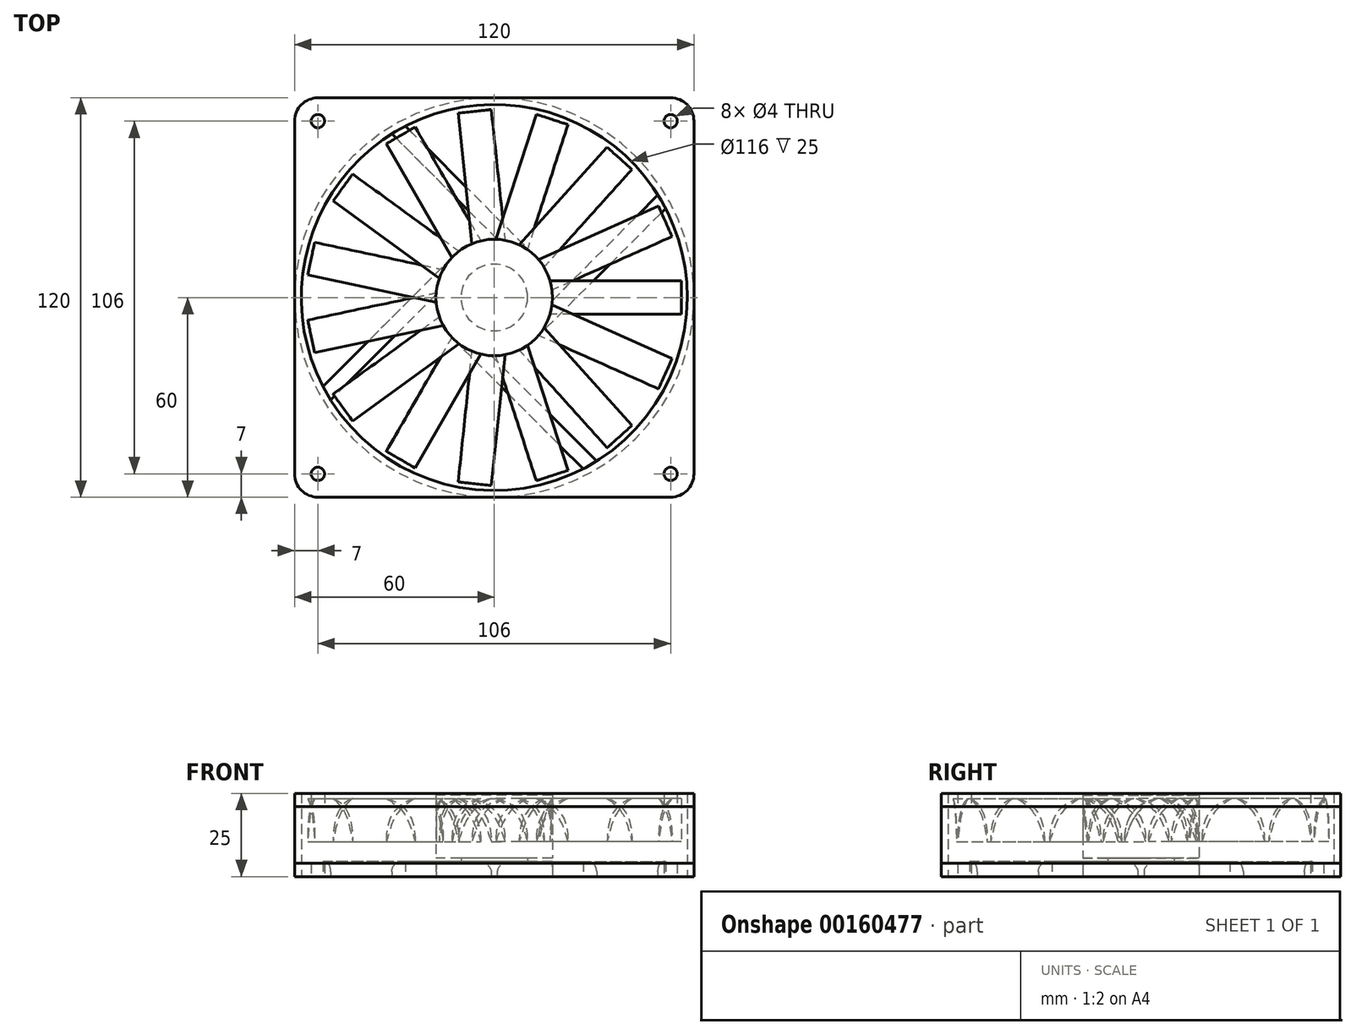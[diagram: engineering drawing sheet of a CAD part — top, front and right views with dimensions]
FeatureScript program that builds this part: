
annotation { "Feature Type Name" : "Feature", "Feature Type Description" : "" }
export const myFeature = defineFeature(function(context is Context, id is Id, definition is map)
    precondition{}
    {
        {
            var Q0;
            Q0=qCreatedBy(makeId("Top.planeOp"),FACE);
            var sketch = newSketch(context, id + "F0", { "sketchPlane" : qUnion([Q0])});
            skLineSegment(sketch, "E0.bottom", {"start": v(-60, 60) * mm, "end": v(60, 60) * mm});
            skLineSegment(sketch, "E0.top", {"start": v(-60, -60) * mm, "end": v(60, -60) * mm});
            skLineSegment(sketch, "E0.left", {"start": v(-60, 60) * mm, "end": v(-60, -60) * mm});
            skLineSegment(sketch, "E0.right", {"start": v(60, 60) * mm, "end": v(60, -60) * mm});
            skCircle(sketch, "E1", {"center": v(0, 0) * mm, "radius": 60 * mm});
            skPoint(sketch, "E2.positionSnap0", {"position": v(0, -60) * mm});
            skPoint(sketch, "E2.positionSnap1", {"position": v(60, 0) * mm});
            skCircle(sketch, "E3", {"center": v(0, 0) * mm, "radius": 58 * mm});
            skSolve(sketch);
        }
        {
            var Q0;
            {var subQ0=sQuery(id+"F0.wireOp",EDGE,"E1");var subQ1=makeQuery(id+"F0.imprint","INTERSECT",VERTEX,{"derivedFrom":[sQuery(id+"F0.wireOp",EDGE,"E0.bottom"),subQ0]});Q0=makeQuery(id+"F0.imprint","IMPRINT",FACE,{"disambiguationData":[TD([[makeQuery(id+"F0.imprint","IMPRINT",EDGE,{"disambiguationData":[TD([[subQ1,1.0]])],"derivedFrom":subQ0}),1.0]])]});}
            extrude(context, id + "F1", {"entities" : qUnion([Q0]), "depth" : 25 * mm});
        }
        {
            var Q0;
            {var subQ0=sQuery(id+"F0.wireOp",EDGE,"E0.left");var subQ1=sQuery(id+"F0.wireOp",EDGE,"E0.bottom");var subQ2=makeQuery(id+"F0.imprint","INTERSECT",VERTEX,{"derivedFrom":[subQ1,subQ0]});Q0=makeQuery(id+"F0.imprint","IMPRINT",FACE,{"disambiguationData":[TD([[makeQuery(id+"F0.imprint","IMPRINT",EDGE,{"disambiguationData":[TD([[subQ2,-1.0]])],"derivedFrom":subQ1}),-1.0]])]});}
            var Q1;
            {var subQ0=sQuery(id+"F0.wireOp",EDGE,"E0.right");var subQ1=sQuery(id+"F0.wireOp",EDGE,"E0.bottom");var subQ2=makeQuery(id+"F0.imprint","INTERSECT",VERTEX,{"derivedFrom":[subQ1,subQ0]});Q1=makeQuery(id+"F0.imprint","IMPRINT",FACE,{"disambiguationData":[TD([[makeQuery(id+"F0.imprint","IMPRINT",EDGE,{"disambiguationData":[TD([[subQ2,1.0]])],"derivedFrom":subQ1}),-1.0]])]});}
            var Q2;
            {var subQ0=sQuery(id+"F0.wireOp",EDGE,"E0.right");var subQ1=sQuery(id+"F0.wireOp",EDGE,"E0.top");var subQ2=makeQuery(id+"F0.imprint","INTERSECT",VERTEX,{"derivedFrom":[subQ1,subQ0]});Q2=makeQuery(id+"F0.imprint","IMPRINT",FACE,{"disambiguationData":[TD([[makeQuery(id+"F0.imprint","IMPRINT",EDGE,{"disambiguationData":[TD([[subQ2,1.0]])],"derivedFrom":subQ1}),1.0]])]});}
            var Q3;
            {var subQ0=sQuery(id+"F0.wireOp",EDGE,"E0.left");var subQ1=sQuery(id+"F0.wireOp",EDGE,"E0.top");var subQ2=makeQuery(id+"F0.imprint","INTERSECT",VERTEX,{"derivedFrom":[subQ1,subQ0]});Q3=makeQuery(id+"F0.imprint","IMPRINT",FACE,{"disambiguationData":[TD([[makeQuery(id+"F0.imprint","IMPRINT",EDGE,{"disambiguationData":[TD([[subQ2,-1.0]])],"derivedFrom":subQ1}),1.0]])]});}
            extrude(context, id + "F2", {"entities" : qUnion([Q0, Q1, Q2, Q3]), "operationType" : NewBodyOperationType.ADD, "depth" : 4 * mm});
        }
        {
            var Q0;
            Q0=makeQuery(id+"F1.opExtrude","CAP_FACE",FACE,{"disambiguationData":[OSD([sQuery(id+"F0.wireOp",EDGE,"E1"),sQuery(id+"F0.wireOp",EDGE,"E3")])],"isStart":false});
            var sketch = newSketch(context, id + "F3", { "sketchPlane" : qUnion([Q0])});
            skLineSegment(sketch, "E4.0", {"start": v(-60, -60) * mm, "end": v(60, -60) * mm});
            skLineSegment(sketch, "E5.0", {"start": v(-60, 60) * mm, "end": v(-60, -60) * mm});
            skLineSegment(sketch, "E6.0", {"start": v(-60, 60) * mm, "end": v(60, 60) * mm});
            skLineSegment(sketch, "E7.0", {"start": v(60, 60) * mm, "end": v(60, -60) * mm});
            skSolve(sketch);
        }
        {
            var Q0;
            {var subQ0=sQuery(id+"F3.wireOp",EDGE,"E7.0");var subQ1=sQuery(id+"F3.wireOp",EDGE,"E4.0");var subQ2=makeQuery(id+"F3.imprint","INTERSECT",VERTEX,{"derivedFrom":[subQ1,subQ0]});Q0=makeQuery(id+"F3.imprint","IMPRINT",FACE,{"disambiguationData":[TD([[makeQuery(id+"F3.imprint","IMPRINT",EDGE,{"disambiguationData":[TD([[subQ2,1.0]])],"derivedFrom":subQ1}),1.0]])]});}
            var Q1;
            {var subQ0=sQuery(id+"F3.wireOp",EDGE,"E7.0");var subQ1=sQuery(id+"F3.wireOp",EDGE,"E6.0");var subQ2=makeQuery(id+"F3.imprint","INTERSECT",VERTEX,{"derivedFrom":[subQ1,subQ0]});Q1=makeQuery(id+"F3.imprint","IMPRINT",FACE,{"disambiguationData":[TD([[makeQuery(id+"F3.imprint","IMPRINT",EDGE,{"disambiguationData":[TD([[subQ2,1.0]])],"derivedFrom":subQ1}),-1.0]])]});}
            var Q2;
            {var subQ0=sQuery(id+"F3.wireOp",EDGE,"E5.0");var subQ1=sQuery(id+"F3.wireOp",EDGE,"E4.0");var subQ2=makeQuery(id+"F3.imprint","INTERSECT",VERTEX,{"derivedFrom":[subQ1,subQ0]});Q2=makeQuery(id+"F3.imprint","IMPRINT",FACE,{"disambiguationData":[TD([[makeQuery(id+"F3.imprint","IMPRINT",EDGE,{"disambiguationData":[TD([[subQ2,-1.0]])],"derivedFrom":subQ1}),1.0]])]});}
            var Q3;
            {var subQ0=sQuery(id+"F3.wireOp",EDGE,"E6.0");var subQ1=sQuery(id+"F3.wireOp",EDGE,"E5.0");var subQ2=makeQuery(id+"F3.imprint","INTERSECT",VERTEX,{"derivedFrom":[subQ1,subQ0]});Q3=makeQuery(id+"F3.imprint","IMPRINT",FACE,{"disambiguationData":[TD([[makeQuery(id+"F3.imprint","IMPRINT",EDGE,{"disambiguationData":[TD([[subQ2,-1.0]])],"derivedFrom":subQ1}),1.0]])]});}
            extrude(context, id + "F4", {"entities" : qUnion([Q0, Q1, Q2, Q3]), "operationType" : NewBodyOperationType.ADD, "oppositeDirection" : true, "depth" : 4 * mm});
        }
        {
            var Q0;
            Q0=makeQuery(id+"F4.opExtrude","SWEPT_EDGE",EDGE,{"disambiguationData":[OSD([sQuery(id+"F3.wireOp",EDGE,"E4.0"),sQuery(id+"F3.wireOp",EDGE,"E5.0")])]});
            var Q1;
            Q1=makeQuery(id+"F2.opExtrude","SWEPT_EDGE",EDGE,{"disambiguationData":[OSD([sQuery(id+"F0.wireOp",EDGE,"E0.top"),sQuery(id+"F0.wireOp",EDGE,"E0.left")])]});
            var Q2;
            Q2=makeQuery(id+"F4.opExtrude","SWEPT_EDGE",EDGE,{"disambiguationData":[OSD([sQuery(id+"F3.wireOp",EDGE,"E5.0"),sQuery(id+"F3.wireOp",EDGE,"E6.0")])]});
            var Q3;
            Q3=makeQuery(id+"F2.opExtrude","SWEPT_EDGE",EDGE,{"disambiguationData":[OSD([sQuery(id+"F0.wireOp",EDGE,"E0.bottom"),sQuery(id+"F0.wireOp",EDGE,"E0.left")])]});
            var Q4;
            Q4=makeQuery(id+"F2.opExtrude","SWEPT_EDGE",EDGE,{"disambiguationData":[OSD([sQuery(id+"F0.wireOp",EDGE,"E0.bottom"),sQuery(id+"F0.wireOp",EDGE,"E0.right")])]});
            var Q5;
            Q5=makeQuery(id+"F4.opExtrude","SWEPT_EDGE",EDGE,{"disambiguationData":[OSD([sQuery(id+"F3.wireOp",EDGE,"E6.0"),sQuery(id+"F3.wireOp",EDGE,"E7.0")])]});
            var Q6;
            Q6=makeQuery(id+"F4.opExtrude","SWEPT_EDGE",EDGE,{"disambiguationData":[OSD([sQuery(id+"F3.wireOp",EDGE,"E4.0"),sQuery(id+"F3.wireOp",EDGE,"E7.0")])]});
            var Q7;
            Q7=makeQuery(id+"F2.opExtrude","SWEPT_EDGE",EDGE,{"disambiguationData":[OSD([sQuery(id+"F0.wireOp",EDGE,"E0.top"),sQuery(id+"F0.wireOp",EDGE,"E0.right")])]});
            fillet(context, id + "F5", {"entities" : qUnion([Q0, Q1, Q2, Q3, Q4, Q5, Q6, Q7]), "radius" : 7 * mm, "tangentPropagation" : true, "allowEdgeOverflow" : false});
        }
        {
            var Q0;
            {var subQ0=sQuery(id+"F0.wireOp",EDGE,"E0.left");var subQ1=sQuery(id+"F0.wireOp",EDGE,"E0.bottom");var subQ2=makeQuery(id+"F0.imprint","INTERSECT",VERTEX,{"derivedFrom":[subQ1,subQ0]});Q0=makeQuery(id+"F0.imprint","IMPRINT",FACE,{"disambiguationData":[TD([[makeQuery(id+"F0.imprint","IMPRINT",EDGE,{"disambiguationData":[TD([[subQ2,-1.0]])],"derivedFrom":subQ1}),-1.0]])]});}
            var sketch = newSketch(context, id + "F6", { "sketchPlane" : qUnion([Q0])});
            skLineSegment(sketch, "E8.bottom", {"start": v(-53, 53) * mm, "end": v(53, 53) * mm, "construction": true});
            skLineSegment(sketch, "E8.top", {"start": v(-53, -53) * mm, "end": v(53, -53) * mm, "construction": true});
            skLineSegment(sketch, "E8.left", {"start": v(-53, 53) * mm, "end": v(-53, -53) * mm, "construction": true});
            skLineSegment(sketch, "E8.right", {"start": v(53, 53) * mm, "end": v(53, -53) * mm, "construction": true});
            skCircle(sketch, "E9", {"center": v(-53, 53) * mm, "radius": 2 * mm});
            skCircle(sketch, "E10", {"center": v(-53, -53) * mm, "radius": 2 * mm});
            skCircle(sketch, "E11", {"center": v(53, -53) * mm, "radius": 2 * mm});
            skCircle(sketch, "E12", {"center": v(53, 53) * mm, "radius": 2 * mm});
            skSolve(sketch);
        }
        {
            var Q0;
            Q0=makeQuery(id+"F6.imprint","IMPRINT",FACE,{"disambiguationData":[TD([[makeQuery(id+"F6.imprint","IMPRINT",EDGE,{"derivedFrom":sQuery(id+"F6.wireOp",EDGE,"E9")}),1.0]])]});
            var Q1;
            Q1=makeQuery(id+"F6.imprint","IMPRINT",FACE,{"disambiguationData":[TD([[makeQuery(id+"F6.imprint","IMPRINT",EDGE,{"derivedFrom":sQuery(id+"F6.wireOp",EDGE,"E10")}),1.0]])]});
            var Q2;
            Q2=makeQuery(id+"F6.imprint","IMPRINT",FACE,{"disambiguationData":[TD([[makeQuery(id+"F6.imprint","IMPRINT",EDGE,{"derivedFrom":sQuery(id+"F6.wireOp",EDGE,"E12")}),1.0]])]});
            var Q3;
            Q3=makeQuery(id+"F6.imprint","IMPRINT",FACE,{"disambiguationData":[TD([[makeQuery(id+"F6.imprint","IMPRINT",EDGE,{"derivedFrom":sQuery(id+"F6.wireOp",EDGE,"E11")}),1.0]])]});
            var Q4;
            Q4=sQuery(id+"F6.wireOp",EDGE,"E9");
            var Q5;
            Q5=sQuery(id+"F6.wireOp",EDGE,"E10");
            var Q6;
            Q6=sQuery(id+"F6.wireOp",EDGE,"E11");
            var Q7;
            Q7=sQuery(id+"F6.wireOp",EDGE,"E12");
            extrude(context, id + "F7", {"entities" : qUnion([Q0, Q1, Q2, Q3]), "operationType" : NewBodyOperationType.REMOVE, "surfaceEntities" : qUnion([Q4, Q5, Q6, Q7]), "depth" : 25 * mm});
        }
        {
            var Q0;
            Q0=qCreatedBy(makeId("Top.planeOp"),FACE);
            var sketch = newSketch(context, id + "F8", { "sketchPlane" : qUnion([Q0])});
            skCircle(sketch, "E13", {"center": v(0, 0) * mm, "radius": 17.5 * mm});
            skLineSegment(sketch, "E14", {"start": v(12.37, 12.37) * mm, "end": v(-26.73, 51.48) * mm});
            skLineSegment(sketch, "E15", {"start": v(0.9, 17.48) * mm, "end": v(-30.78, 49.16) * mm});
            skLineSegment(sketch, "E16.1.0", {"start": v(-17.48, 0.9) * mm, "end": v(-49.16, -30.78) * mm});
            skLineSegment(sketch, "E16.1.1", {"start": v(-12.37, 12.37) * mm, "end": v(-51.48, -26.73) * mm});
            skLineSegment(sketch, "E16.2.0", {"start": v(-0.9, -17.48) * mm, "end": v(30.78, -49.16) * mm});
            skLineSegment(sketch, "E16.2.1", {"start": v(-12.37, -12.37) * mm, "end": v(26.73, -51.48) * mm});
            skLineSegment(sketch, "E16.3.0", {"start": v(17.48, -0.9) * mm, "end": v(49.16, 30.78) * mm});
            skLineSegment(sketch, "E16.3.1", {"start": v(12.37, -12.37) * mm, "end": v(51.48, 26.73) * mm});
            skCircle(sketch, "E17", {"center": v(0, 0) * mm, "radius": 58 * mm});
            skSolve(sketch);
        }
        {
            var Q0;
            {var subQ0=sQuery(id+"F8.wireOp",EDGE,"E14");Q0=makeQuery(id+"F8.imprint","IMPRINT",FACE,{"disambiguationData":[TD([[makeQuery(id+"F8.imprint","IMPRINT",EDGE,{"derivedFrom":subQ0}),1.0]])]});}
            var Q1;
            {var subQ0=sQuery(id+"F8.wireOp",EDGE,"E16.1.0");Q1=makeQuery(id+"F8.imprint","IMPRINT",FACE,{"disambiguationData":[TD([[makeQuery(id+"F8.imprint","IMPRINT",EDGE,{"derivedFrom":subQ0}),-1.0]])]});}
            var Q2;
            {var subQ0=sQuery(id+"F8.wireOp",EDGE,"E13");var subQ5=makeQuery(id+"F8.imprint","INTERSECT",VERTEX,{"derivedFrom":[subQ0,sQuery(id+"F8.wireOp",EDGE,"E14")]});Q2=makeQuery(id+"F8.imprint","IMPRINT",FACE,{"disambiguationData":[TD([[makeQuery(id+"F8.imprint","IMPRINT",EDGE,{"disambiguationData":[TD([[subQ5,-1.0]])],"derivedFrom":subQ0}),1.0]])]});}
            var Q3;
            {var subQ0=sQuery(id+"F8.wireOp",EDGE,"E16.3.0");Q3=makeQuery(id+"F8.imprint","IMPRINT",FACE,{"disambiguationData":[TD([[makeQuery(id+"F8.imprint","IMPRINT",EDGE,{"derivedFrom":subQ0}),-1.0]])]});}
            var Q4;
            {var subQ0=sQuery(id+"F8.wireOp",EDGE,"E16.2.0");Q4=makeQuery(id+"F8.imprint","IMPRINT",FACE,{"disambiguationData":[TD([[makeQuery(id+"F8.imprint","IMPRINT",EDGE,{"derivedFrom":subQ0}),-1.0]])]});}
            extrude(context, id + "F9", {"entities" : qUnion([Q0, Q1, Q2, Q3, Q4]), "operationType" : NewBodyOperationType.ADD, "depth" : 4.5 * mm});
        }
        {
            var Q0;
            Q0=makeQuery(id+"F9.opExtrude","CAP_FACE",FACE,{"disambiguationData":[OSD([sQuery(id+"F8.wireOp",EDGE,"E13"),sQuery(id+"F8.wireOp",EDGE,"E14"),sQuery(id+"F8.wireOp",EDGE,"E15"),sQuery(id+"F8.wireOp",EDGE,"E16.1.0"),sQuery(id+"F8.wireOp",EDGE,"E16.1.1"),sQuery(id+"F8.wireOp",EDGE,"E16.2.0"),sQuery(id+"F8.wireOp",EDGE,"E16.2.1"),sQuery(id+"F8.wireOp",EDGE,"E16.3.0"),sQuery(id+"F8.wireOp",EDGE,"E16.3.1"),sQuery(id+"F8.wireOp",EDGE,"E17")])],"isStart":false});
            var sketch = newSketch(context, id + "F10", { "sketchPlane" : qUnion([Q0])});
            skCircle(sketch, "E18", {"center": v(0, 0) * mm, "radius": 10 * mm});
            skSolve(sketch);
        }
        {
            var Q0;
            Q0=makeQuery(id+"F9.opExtrude","CAP_FACE",FACE,{"disambiguationData":[OSD([sQuery(id+"F8.wireOp",EDGE,"E13"),sQuery(id+"F8.wireOp",EDGE,"E14"),sQuery(id+"F8.wireOp",EDGE,"E15"),sQuery(id+"F8.wireOp",EDGE,"E16.1.0"),sQuery(id+"F8.wireOp",EDGE,"E16.1.1"),sQuery(id+"F8.wireOp",EDGE,"E16.2.0"),sQuery(id+"F8.wireOp",EDGE,"E16.2.1"),sQuery(id+"F8.wireOp",EDGE,"E16.3.0"),sQuery(id+"F8.wireOp",EDGE,"E16.3.1"),sQuery(id+"F8.wireOp",EDGE,"E17")])],"isStart":false});
            cPlane(context, id + "F11", {"entities" : qUnion([Q0]), "cplaneType" : CPlaneType.OFFSET, "offset" : 1 * mm, "width" : 150 * mm, "height" : 150 * mm});
        }
        {
            var Q0;
            Q0=qCreatedBy(id+"F11.planeOp",FACE);
            var sketch = newSketch(context, id + "F12", { "sketchPlane" : qUnion([Q0])});
            skCircle(sketch, "E19", {"center": v(0, 0) * mm, "radius": 17.5 * mm});
            skSolve(sketch);
        }
        {
            var Q0;
            Q0=makeQuery(id+"F12.imprint","IMPRINT",FACE,{"disambiguationData":[TD([[makeQuery(id+"F12.imprint","IMPRINT",EDGE,{"derivedFrom":sQuery(id+"F12.wireOp",EDGE,"E19")}),1.0]])]});
            extrude(context, id + "F13", {"entities" : qUnion([Q0]), "depth" : 19 * mm});
        }
        {
            var Q0;
            Q0=qCreatedBy(makeId("Right.planeOp"),FACE);
            var sketch = newSketch(context, id + "F14", { "sketchPlane" : qUnion([Q0])});
            skFitSpline(sketch, "E20", {"points": [v(5, 23.5) * mm, v(-5, 10.5) * mm], "startDerivative": vector(-15, -3.76) * mm, "endDerivative": vector(0.25, -27.3) * mm});
            skFitSpline(sketch, "E21", {"points": [v(5, 23.5) * mm, v(-5, 10.5) * mm], "startDerivative": vector(-19.69, -10) * mm, "endDerivative": vector(-7.2, -21.55) * mm});
            skSolve(sketch);
        }
        {
            var Q0;
            Q0=makeQuery(id+"F14.imprint","IMPRINT",FACE,{"disambiguationData":[TD([[makeQuery(id+"F14.imprint","IMPRINT",EDGE,{"derivedFrom":sQuery(id+"F14.wireOp",EDGE,"E20")}),1.0]])]});
            extrude(context, id + "F15", {"entities" : qUnion([Q0]), "operationType" : NewBodyOperationType.ADD, "depth" : 56.25 * mm});
        }
        {
            var Q0;
            Q0=makeQuery(id+"F13.opExtrude","SWEPT_BODY",BODY,{"disambiguationData":[OSD([sQuery(id+"F12.wireOp",EDGE,"E19")])]});
            var Q1;
            Q1=makeQuery(id+"F13.opExtrude","CAP_EDGE",EDGE,{"disambiguationData":[OSD([sQuery(id+"F12.wireOp",EDGE,"E19")])],"isStart":true});
            circularPattern(context, id + "F16", {"operationType" : NewBodyOperationType.ADD, "entities" : qUnion([Q0]), "axis" : qUnion([Q1]), "angle" : 24 * degree, "instanceCount" : 15});
        }
        {
            var Q0;
            Q0=makeQuery(id+"F10.imprint","IMPRINT",FACE,{"disambiguationData":[TD([[makeQuery(id+"F10.imprint","IMPRINT",EDGE,{"derivedFrom":sQuery(id+"F10.wireOp",EDGE,"E18")}),1.0]])]});
            extrude(context, id + "F17", {"entities" : qUnion([Q0]), "operationType" : NewBodyOperationType.ADD, "depth" : 5 * mm});
        }
        {
            var Q0;
            Q0=makeQuery(id+"F9.opExtrude","CAP_EDGE",EDGE,{"disambiguationData":[OSD([sQuery(id+"F8.wireOp",EDGE,"E15")])],"isStart":false});
            var Q1;
            Q1=makeQuery(id+"F9.opExtrude","CAP_EDGE",EDGE,{"disambiguationData":[OSD([sQuery(id+"F8.wireOp",EDGE,"E16.1.0")])],"isStart":false});
            var Q2;
            Q2=makeQuery(id+"F9.opExtrude","CAP_EDGE",EDGE,{"disambiguationData":[OSD([sQuery(id+"F8.wireOp",EDGE,"E16.2.0")])],"isStart":false});
            var Q3;
            Q3=makeQuery(id+"F9.opExtrude","CAP_EDGE",EDGE,{"disambiguationData":[OSD([sQuery(id+"F8.wireOp",EDGE,"E16.3.0")])],"isStart":false});
            fillet(context, id + "F18", {"entities" : qUnion([Q0, Q1, Q2, Q3]), "radius" : 3 * mm, "tangentPropagation" : true, "allowEdgeOverflow" : false});
        }
    });
